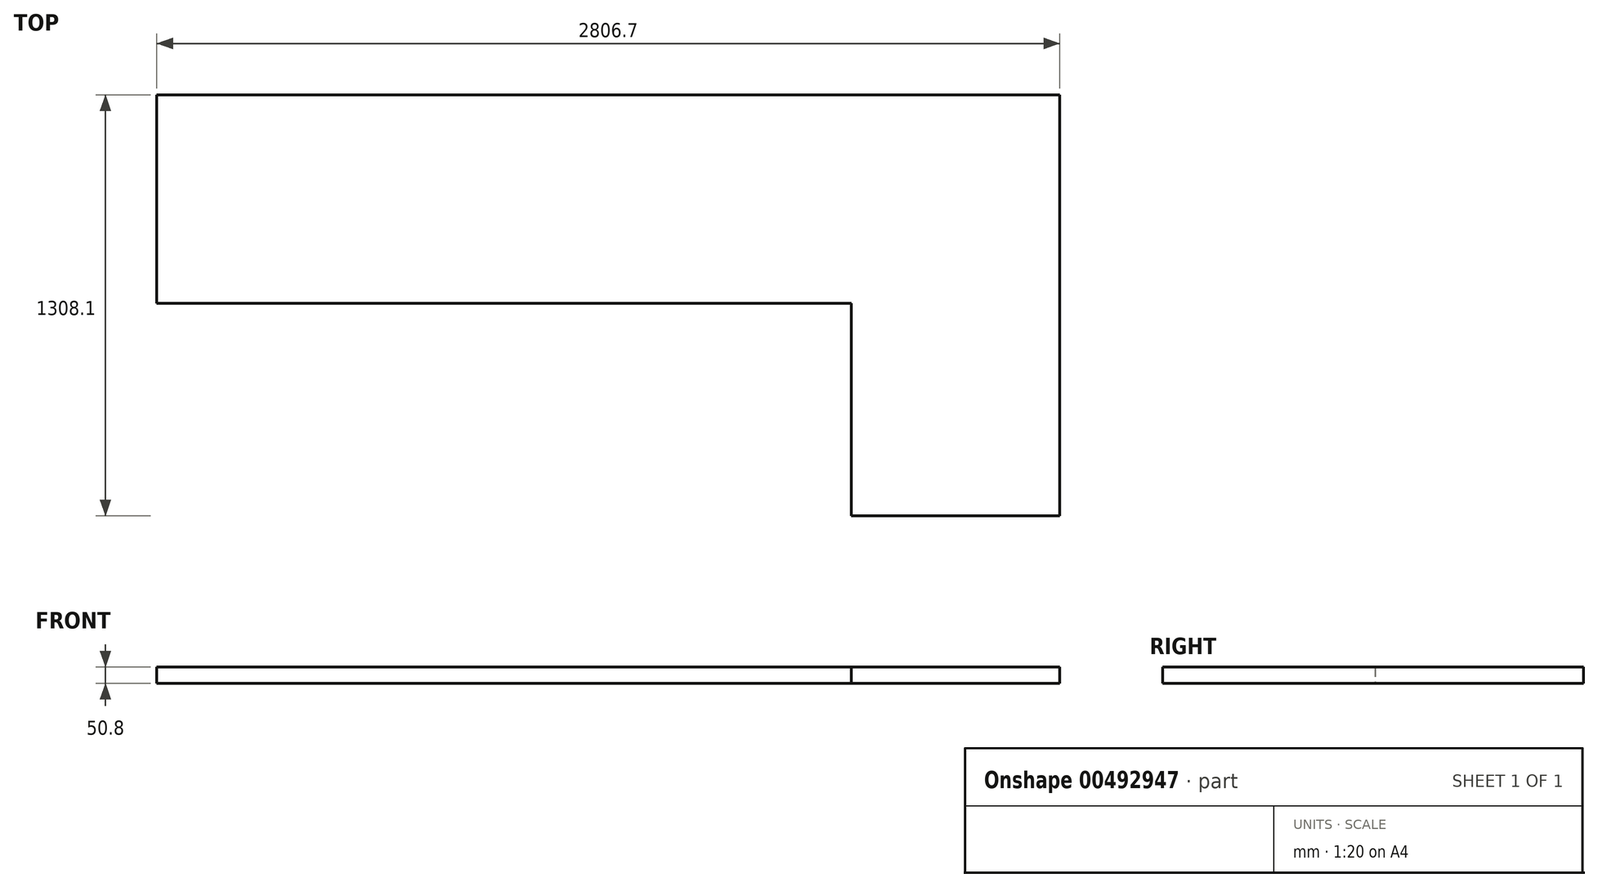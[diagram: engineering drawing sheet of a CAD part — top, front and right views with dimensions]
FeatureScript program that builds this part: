
annotation { "Feature Type Name" : "Feature", "Feature Type Description" : "" }
export const myFeature = defineFeature(function(context is Context, id is Id, definition is map)
    precondition{}
    {
        {
            var Q0;
            Q0=qCreatedBy(makeId("Top.planeOp"),FACE);
            var sketch = newSketch(context, id + "F0", { "sketchPlane" : qUnion([Q0])});
            skLineSegment(sketch, "E0.bottom", {"start": v(0, -323.85) * mm, "end": v(-2159, -323.85) * mm});
            skLineSegment(sketch, "E0.top", {"start": v(0, 323.85) * mm, "end": v(-2159, 323.85) * mm});
            skLineSegment(sketch, "E0.left", {"start": v(0, 0) * mm, "end": v(0, 323.85) * mm});
            skLineSegment(sketch, "E0.right", {"start": v(-2159, -323.85) * mm, "end": v(-2159, 323.85) * mm});
            skLineSegment(sketch, "E1.bottom", {"start": v(0, 323.85) * mm, "end": v(647.7, 323.85) * mm});
            skLineSegment(sketch, "E1.top", {"start": v(0, -984.25) * mm, "end": v(647.7, -984.25) * mm});
            skLineSegment(sketch, "E1.left", {"start": v(0, 323.85) * mm, "end": v(0, -984.25) * mm});
            skLineSegment(sketch, "E1.right", {"start": v(647.7, 323.85) * mm, "end": v(647.7, -984.25) * mm});
            skLineSegment(sketch, "E2", {"start": v(-2159, 0) * mm, "end": v(0, 0) * mm, "construction": true});
            skSolve(sketch);
        }
        {
            var Q0;
            Q0=makeQuery(id+"F0.imprint","IMPRINT",FACE,{"disambiguationData":[TD([[makeQuery(id+"F0.imprint","IMPRINT",EDGE,{"derivedFrom":sQuery(id+"F0.wireOp",EDGE,"E0.bottom")}),-1.0]])]});
            var Q1;
            Q1=makeQuery(id+"F0.imprint","IMPRINT",FACE,{"disambiguationData":[TD([[makeQuery(id+"F0.imprint","IMPRINT",EDGE,{"derivedFrom":sQuery(id+"F0.wireOp",EDGE,"E0.left")}),-1.0]])]});
            extrude(context, id + "F1", {"entities" : qUnion([Q0, Q1]), "depth" : 50.8 * mm, "offsetDistance" : 25.4 * mm});
        }
    });
